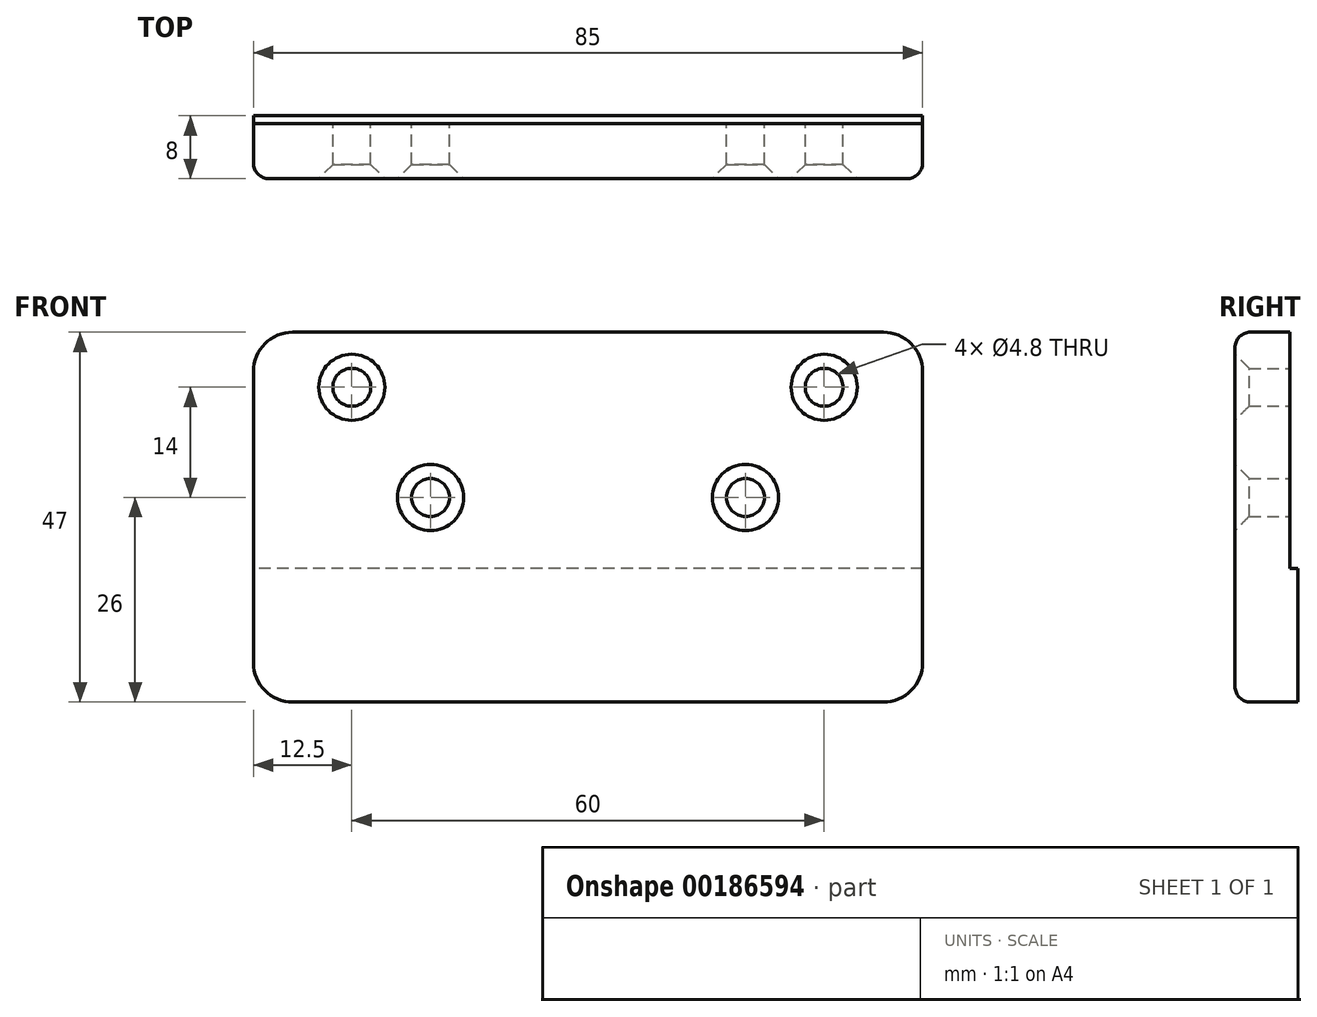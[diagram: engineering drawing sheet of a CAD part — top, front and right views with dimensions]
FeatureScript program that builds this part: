
annotation { "Feature Type Name" : "Feature", "Feature Type Description" : "" }
export const myFeature = defineFeature(function(context is Context, id is Id, definition is map)
    precondition{}
    {
        {
            var Q0;
            Q0=qCreatedBy(makeId("Front.planeOp"),FACE);
            var sketch = newSketch(context, id + "F0", { "sketchPlane" : qUnion([Q0])});
            skLineSegment(sketch, "E0.bottom", {"start": v(42.5, 23.5) * mm, "end": v(-42.5, 23.5) * mm});
            skLineSegment(sketch, "E0.top", {"start": v(42.5, -23.5) * mm, "end": v(-42.5, -23.5) * mm});
            skLineSegment(sketch, "E0.left", {"start": v(42.5, 23.5) * mm, "end": v(42.5, -23.5) * mm});
            skLineSegment(sketch, "E0.right", {"start": v(-42.5, 23.5) * mm, "end": v(-42.5, -23.5) * mm});
            skPoint(sketch, "E0.middle", {"position": v(0, 0) * mm});
            skCircle(sketch, "E1", {"center": v(-30, 16.5) * mm, "radius": 2.4 * mm});
            skCircle(sketch, "E2", {"center": v(-20, 2.5) * mm, "radius": 2.4 * mm});
            skCircle(sketch, "E3.MirrorC", {"center": v(30, 16.5) * mm, "radius": 2.4 * mm});
            skCircle(sketch, "E4.MirrorC", {"center": v(20, 2.5) * mm, "radius": 2.4 * mm});
            skLineSegment(sketch, "E5", {"start": v(-20, 2.5) * mm, "end": v(-20, -23.5) * mm});
            skSolve(sketch);
        }
        {
            var Q0;
            Q0=qSketchRegion(id+"F0",true);
            extrude(context, id + "F1", {"entities" : qUnion([Q0]), "depth" : 7 * mm});
        }
        {
            var Q0;
            Q0=makeQuery(id+"F1.opExtrude","CAP_FACE",FACE,{"disambiguationData":[OSD([sQuery(id+"F0.wireOp",EDGE,"E0.bottom"),sQuery(id+"F0.wireOp",EDGE,"E0.top"),sQuery(id+"F0.wireOp",EDGE,"E0.left"),sQuery(id+"F0.wireOp",EDGE,"E0.right"),sQuery(id+"F0.wireOp",EDGE,"E1"),sQuery(id+"F0.wireOp",EDGE,"E2"),sQuery(id+"F0.wireOp",EDGE,"E3.MirrorC"),sQuery(id+"F0.wireOp",EDGE,"E4.MirrorC")])],"isStart":true});
            var sketch = newSketch(context, id + "F2", { "sketchPlane" : qUnion([Q0])});
            skLineSegment(sketch, "E6.bottom", {"start": v(-42.5, -23.5) * mm, "end": v(42.5, -23.5) * mm});
            skLineSegment(sketch, "E6.top", {"start": v(-42.5, -6.5) * mm, "end": v(42.5, -6.5) * mm});
            skLineSegment(sketch, "E6.left", {"start": v(-42.5, -23.5) * mm, "end": v(-42.5, -6.5) * mm});
            skLineSegment(sketch, "E6.right", {"start": v(42.5, -23.5) * mm, "end": v(42.5, -6.5) * mm});
            skSolve(sketch);
        }
        {
            var Q0;
            Q0=qSketchRegion(id+"F2",true);
            extrude(context, id + "F3", {"entities" : qUnion([Q0]), "operationType" : NewBodyOperationType.ADD, "depth" : 1 * mm});
        }
        {
            var Q0;
            Q0=makeQuery(id+"F1.opExtrude","SWEPT_EDGE",EDGE,{"disambiguationData":[OSD([sQuery(id+"F0.wireOp",EDGE,"E0.bottom"),sQuery(id+"F0.wireOp",EDGE,"E0.left")])]});
            var Q1;
            Q1=makeQuery(id+"F1.opExtrude","SWEPT_EDGE",EDGE,{"disambiguationData":[OSD([sQuery(id+"F0.wireOp",EDGE,"E0.bottom"),sQuery(id+"F0.wireOp",EDGE,"E0.right")])]});
            var Q2;
            Q2=makeQuery(id+"F3.boolean.opBoolean","MERGE",EDGE,{"derivedFrom":[makeQuery(id+"F1.opExtrude","SWEPT_EDGE",EDGE,{"disambiguationData":[OSD([sQuery(id+"F0.wireOp",EDGE,"E0.top"),sQuery(id+"F0.wireOp",EDGE,"E0.left")])]}),makeQuery(id+"F3.opExtrude","SWEPT_EDGE",EDGE,{"disambiguationData":[OSD([sQuery(id+"F2.wireOp",EDGE,"E6.bottom"),sQuery(id+"F2.wireOp",EDGE,"E6.left")])]})]});
            var Q3;
            Q3=makeQuery(id+"F3.boolean.opBoolean","MERGE",EDGE,{"derivedFrom":[makeQuery(id+"F1.opExtrude","SWEPT_EDGE",EDGE,{"disambiguationData":[OSD([sQuery(id+"F0.wireOp",EDGE,"E0.top"),sQuery(id+"F0.wireOp",EDGE,"E0.right")])]}),makeQuery(id+"F3.opExtrude","SWEPT_EDGE",EDGE,{"disambiguationData":[OSD([sQuery(id+"F2.wireOp",EDGE,"E6.bottom"),sQuery(id+"F2.wireOp",EDGE,"E6.right")])]})]});
            fillet(context, id + "F4", {"entities" : qUnion([Q0, Q1, Q2, Q3]), "radius" : 5 * mm, "tangentPropagation" : true, "allowEdgeOverflow" : false});
        }
        {
            var Q0;
            Q0=makeQuery(id+"F1.opExtrude","CAP_EDGE",EDGE,{"disambiguationData":[OSD([sQuery(id+"F0.wireOp",EDGE,"E0.top")])],"isStart":false});
            fillet(context, id + "F5", {"entities" : qUnion([Q0]), "radius" : 2 * mm, "tangentPropagation" : true, "allowEdgeOverflow" : false});
        }
        {
            var Q0;
            Q0=makeQuery(id+"F1.opExtrude","CAP_EDGE",EDGE,{"disambiguationData":[OSD([sQuery(id+"F0.wireOp",EDGE,"E4.MirrorC")])],"isStart":false});
            var Q1;
            Q1=makeQuery(id+"F1.opExtrude","CAP_EDGE",EDGE,{"disambiguationData":[OSD([sQuery(id+"F0.wireOp",EDGE,"E3.MirrorC")])],"isStart":false});
            var Q2;
            Q2=makeQuery(id+"F1.opExtrude","CAP_EDGE",EDGE,{"disambiguationData":[OSD([sQuery(id+"F0.wireOp",EDGE,"E2")])],"isStart":false});
            var Q3;
            Q3=makeQuery(id+"F1.opExtrude","CAP_EDGE",EDGE,{"disambiguationData":[OSD([sQuery(id+"F0.wireOp",EDGE,"E1")])],"isStart":false});
            chamfer(context, id + "F6", {"entities" : qUnion([Q0, Q1, Q2, Q3]), "width" : 1.8 * mm, "tangentPropagation" : true});
        }
    });
